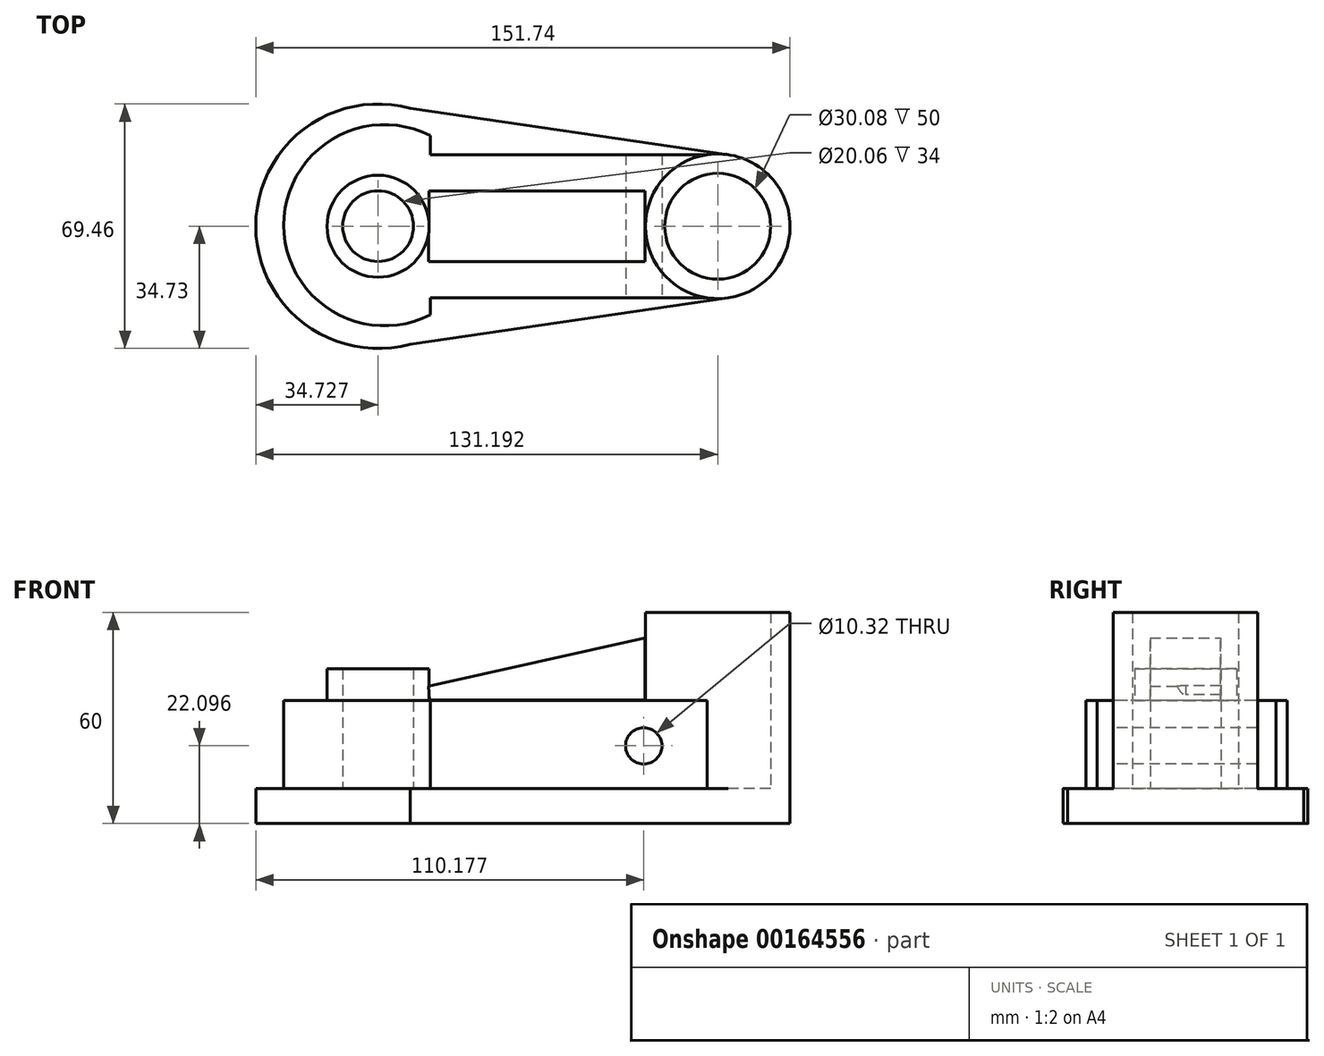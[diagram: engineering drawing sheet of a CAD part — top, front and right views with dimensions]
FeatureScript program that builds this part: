
annotation { "Feature Type Name" : "Feature", "Feature Type Description" : "" }
export const myFeature = defineFeature(function(context is Context, id is Id, definition is map)
    precondition{}
    {
        {
            var Q0;
            Q0=qCreatedBy(makeId("Top.planeOp"),FACE);
            var sketch = newSketch(context, id + "F0", { "sketchPlane" : qUnion([Q0])});
            skCircle(sketch, "E0", {"center": v(-48.23, 0) * mm, "radius": 34.73 * mm});
            skCircle(sketch, "E1", {"center": v(48.23, 0) * mm, "radius": 20.54 * mm});
            skLineSegment(sketch, "E2", {"start": v(-47.35, 34.72) * mm, "end": v(51.2, 20.33) * mm});
            skLineSegment(sketch, "E3", {"start": v(-47.35, -34.72) * mm, "end": v(51.2, -20.33) * mm});
            skSolve(sketch);
        }
        {
            var Q0;
            Q0 = qSketchRegion(id + "F0", true);
            extrude(context, id + "F1", {"entities" : qUnion([Q0]), "depth" : 10 * mm});
        }
        {
            var Q0;
            Q0=makeQuery(id+"F1.opExtrude","CAP_FACE",FACE,{"disambiguationData":[OSD([sQuery(id+"F0.wireOp",EDGE,"E0"),sQuery(id+"F0.wireOp",EDGE,"E1"),sQuery(id+"F0.wireOp",EDGE,"E2"),sQuery(id+"F0.wireOp",EDGE,"E3")])],"isStart":false});
            var sketch = newSketch(context, id + "F2", { "sketchPlane" : qUnion([Q0])});
            skCircle(sketch, "E4", {"center": v(48.23, 0) * mm, "radius": 20.54 * mm});
            skCircle(sketch, "E5", {"center": v(48.23, 0) * mm, "radius": 15.04 * mm});
            skSolve(sketch);
        }
        {
            var Q0;
            Q0 = qSketchRegion(id + "F2", true);
            extrude(context, id + "F3", {"entities" : qUnion([Q0]), "operationType" : NewBodyOperationType.ADD, "depth" : 50 * mm});
        }
        {
            var Q0;
            {var subQ0=sQuery(id+"F0.wireOp",EDGE,"E3");var subQ1=sQuery(id+"F0.wireOp",EDGE,"E2");var subQ2=sQuery(id+"F0.wireOp",EDGE,"E1");var subQ3=sQuery(id+"F0.wireOp",EDGE,"E0");Q0=makeQuery(id+"F3.boolean.opBoolean","SPLIT",FACE,{"disambiguationData":[TD([makeQuery(id+"F1.opExtrude","SWEPT_FACE",FACE,{"disambiguationData":[OSD([subQ3])]})])],"derivedFrom":makeQuery(id+"F1.opExtrude","CAP_FACE",FACE,{"disambiguationData":[OSD([subQ3,subQ2,subQ1,subQ0])],"isStart":false})});}
            var sketch = newSketch(context, id + "F4", { "sketchPlane" : qUnion([Q0])});
            skCircle(sketch, "E6", {"center": v(-48.23, 0) * mm, "radius": 14.49 * mm});
            skCircle(sketch, "E7", {"center": v(-48.23, 0) * mm, "radius": 10.03 * mm});
            skSolve(sketch);
        }
        {
            var Q0;
            Q0 = qSketchRegion(id + "F4", true);
            extrude(context, id + "F5", {"entities" : qUnion([Q0]), "operationType" : NewBodyOperationType.ADD, "depth" : 34 * mm});
        }
        {
            var Q0;
            {var subQ0=sQuery(id+"F0.wireOp",EDGE,"E3");var subQ3=sQuery(id+"F0.wireOp",EDGE,"E2");var subQ5=sQuery(id+"F0.wireOp",EDGE,"E1");var subQ7=sQuery(id+"F0.wireOp",EDGE,"E0");var subQ8=makeQuery(id+"F1.opExtrude","SWEPT_FACE",FACE,{"disambiguationData":[OSD([subQ7])]});Q0=makeQuery(id+"F5.boolean.opBoolean","SPLIT",FACE,{"disambiguationData":[TD([subQ8])],"derivedFrom":makeQuery(id+"F3.boolean.opBoolean","SPLIT",FACE,{"disambiguationData":[TD([subQ8])],"derivedFrom":makeQuery(id+"F1.opExtrude","CAP_FACE",FACE,{"disambiguationData":[OSD([subQ7,subQ5,subQ3,subQ0])],"isStart":false})})});}
            var sketch = newSketch(context, id + "F6", { "sketchPlane" : qUnion([Q0])});
            skLineSegment(sketch, "E8", {"start": v(51.2, 20.33) * mm, "end": v(-33.44, 20.33) * mm});
            skLineSegment(sketch, "E9", {"start": v(51.2, -20.33) * mm, "end": v(-33.44, -20.33) * mm});
            skLineSegment(sketch, "E10", {"start": v(-33.44, -20.33) * mm, "end": v(-33.44, -25.16) * mm});
            skLineSegment(sketch, "E11", {"start": v(-33.44, 20.33) * mm, "end": v(-33.44, 25.75) * mm});
            skArc(sketch, "E12", {"start": v(-33.44, 25.75) * mm, "mid": v(-75, 0.3) * mm, "end": v(-33.44, -25.16) * mm});
            skArc(sketch, "E13", {"start": v(51.2, 20.33) * mm, "mid": v(27.69, 0) * mm, "end": v(51.2, -20.33) * mm});
            skArc(sketch, "E14", {"start": v(51.2, 20.33) * mm, "mid": v(30.87, 0) * mm, "end": v(51.2, -20.33) * mm});
            skSolve(sketch);
        }
        {
            var Q0;
            {var subQ0=sQuery(id+"F6.wireOp",EDGE,"E10");Q0=makeQuery(id+"F6.imprint","IMPRINT",FACE,{"disambiguationData":[TD([[makeQuery(id+"F6.imprint","IMPRINT",EDGE,{"derivedFrom":subQ0}),-1.0]])]});}
            extrude(context, id + "F7", {"entities" : qUnion([Q0]), "operationType" : NewBodyOperationType.ADD, "depth" : 25 * mm});
        }
        {
            var Q0;
            Q0=qCreatedBy(makeId("Front.planeOp"),FACE);
            var sketch = newSketch(context, id + "F8", { "sketchPlane" : qUnion([Q0])});
            skLineSegment(sketch, "E15", {"start": v(-33.62, 35.13) * mm, "end": v(27.57, 35.13) * mm});
            skLineSegment(sketch, "E16", {"start": v(27.57, 35.13) * mm, "end": v(27.57, 52.8) * mm});
            skLineSegment(sketch, "E17", {"start": v(27.57, 52.8) * mm, "end": v(-33.94, 39.08) * mm});
            skLineSegment(sketch, "E18", {"start": v(-33.94, 39.08) * mm, "end": v(-33.62, 35.13) * mm});
            skSolve(sketch);
        }
        {
            var Q0;
            Q0 = qSketchRegion(id + "F8", true);
            extrude(context, id + "F9", {"entities" : qUnion([Q0]), "operationType" : NewBodyOperationType.ADD, "depth" : 10 * mm});
        }
        {
            var Q0;
            Q0=makeQuery(id+"F9.opExtrude","CAP_FACE",FACE,{"disambiguationData":[OSD([sQuery(id+"F8.wireOp",EDGE,"E15"),sQuery(id+"F8.wireOp",EDGE,"E16"),sQuery(id+"F8.wireOp",EDGE,"E17"),sQuery(id+"F8.wireOp",EDGE,"E18")])],"isStart":true});
            extrude(context, id + "F10", {"entities" : qUnion([Q0]), "operationType" : NewBodyOperationType.ADD, "depth" : 10 * mm});
        }
        {
            var Q0;
            Q0=makeQuery(id+"F7.opExtrude","SWEPT_FACE",FACE,{"disambiguationData":[OSD([sQuery(id+"F6.wireOp",EDGE,"E9")])]});
            var sketch = newSketch(context, id + "F11", { "sketchPlane" : qUnion([Q0])});
            skCircle(sketch, "E19", {"center": v(27.22, 22.1) * mm, "radius": 5.16 * mm});
            skSolve(sketch);
        }
        {
            var Q0;
            Q0 = qSketchRegion(id + "F11", true);
            extrude(context, id + "F12", {"entities" : qUnion([Q0]), "operationType" : NewBodyOperationType.REMOVE, "oppositeDirection" : true, "depth" : 111 * mm});
        }
    });
